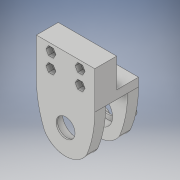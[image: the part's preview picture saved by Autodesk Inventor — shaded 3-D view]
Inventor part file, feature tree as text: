
AUTODESK INVENTOR PART (.ipt)
format: ipt  version: 2019 (Build 230136000, 136)  size: 302,080 bytes
history: native  units: mm
features: sketch x12, extrude x9, chamfer x4, hole x3, plane x1, fillet x1
ambient origin geometry x8: Origin, YZ Plane, XZ Plane, XY Plane, X Axis, Y Axis, Z Axis, Center Point
bodies: Solid1 (feature_tree)
feature tree (30):
  extrude  "Extrusion1"  Depth=20.0mm
  extrude  "Extrusion2"  Depth=40.0mm
  hole  "Hole1"  [1 undecoded]
  plane  "Work Plane1"
  extrude  "Extrusion3"  Depth=30.0mm TaperAngle=360.0deg
  extrude  "Extrusion4"  Depth=10.0mm TaperAngle=0.0deg
  hole  "Hole2"  [1 undecoded]
  extrude  "Extrusion5"  Depth=10.0mm
  extrude  "Extrusion6"  Depth=5.9mm
  chamfer  "Chamfer2"  Distance=3.5mm
  fillet  "Fillet1"  Radius=17.0mm
  extrude  "Extrusion7"  Depth=10.0mm TaperAngle=45.0deg
  chamfer  "Chamfer3"  Distance=74.25mm
  chamfer  "Chamfer4"  Distance=10.0mm
  extrude  "Extrusion8"  Depth=10.0mm TaperAngle=45.0deg
  extrude  "Extrusion9"  Depth=4.0mm TaperAngle=45.0deg
  chamfer  "Chamfer5"  Distance=1.0mm
  hole  "Hole3"  [1 undecoded]
  sketch  "Sketch1"  dims[d0=19.5mm d2=20.0mm]
  sketch  "Sketch2"  dims[d3=45.0mm d4=40.0mm]
  sketch  "Sketch3"  dims[d5=30.0mm d6=0.0mm d7=25.0mm]
  sketch  "Sketch4"  dims[d8=6.0mm d9=30.0mm d11=360.0deg]
  sketch  "Sketch5"  dims[d13=3.5mm d14=0.0mm]
  sketch  "Sketch6"  dims[d15=3.9mm d16=6.0mm d17=5.0mm d18=5.0mm d19=90.0deg d20=10.0mm d21=0.0mm d22=15.0mm d23=0.0mm]
  sketch  "Sketch7"  dims[d27=20.0mm d28=15.0mm d29=0.0mm]
  sketch  "Sketch8"  dims[d30=20.0mm]
  sketch  "Sketch10"  dims[d31=3.75mm d32=6.0mm d33=4.0mm d34=2.0mm d35=90.0deg d36=10.0mm d37=90.0deg d38=5.9mm]
  sketch  "Sketch11"  dims[d39=5.9mm d40=5.9mm]
  sketch  "Sketch12"  dims[d41=5.9mm d42=3.5mm d43=0.0mm d44=17.0mm]
  sketch  "Sketch13"  dims[d45=10.0mm d46=0.0mm d47=8.25mm d48=2.0mm d49=45.0deg d50=74.25mm d51=10.0mm d52=0.0mm d53=9.17mm d54=2.0mm d55=45.0deg d56=4.0mm d57=2.0mm d58=45.0deg d59=1.0mm d60=0.0mm d61=1.0mm d62=0.0mm d63=2.0mm d64=2.0mm d65=45.0deg d66=13.0mm d67=6.0mm d68=10.0mm d69=7.0mm d70=90.0deg d71=8.0mm d72=20.594885mm]
note: 3 required parameter values undecoded (feature->parameter linkage not recoverable at this tier; creation-order binding heuristic only, values carry confidence <= 0.55)
